# Revit family: Sarlam_Lighting_Bollard_light_Chartres_Infini_T1_vandal_resistant_Diam_322mm_2000Lm
name_source: partatom
category: Luminaires
units: mm (PartAtom-declared; Revit-internal decimal feet)

## family parameters
Basée sur le plan de construction = Non
Cote de connecteur circulaire = Utiliser le diamètre
Couper avec des vides une fois chargée = Non
Partagée = Non
Point de calcul de pièce = Non
Source d'éclairage = Non
Toujours verticalement = Oui
Type d'élément = Normal

## types (28) — shared parameters
Colour rendering index CRI = 80-89
Colour temperature K MAX = 4000
Colour temperature K MIN = 4000
Effective luminous flux lm = 2000
Fabricant = LEGRAND
General Conditions of Use = https://export.legrand.com
Height/depth = 70 mm  [stored 0.229659 ft]
Lamp holder = None
Lamp power at multiwatt = 21/39W
Lamp type = LED not exchangeable
Length = 322 mm  [stored 1.05643 ft]
Light sharing = Symmetric
Material housing = Plastique
Nominal voltage (Un) V MAX = 253
Nominal voltage (Un) V MIN = 207
Outer diameter = 322 mm  [stored 1.05643 ft]
Protection Class = II
Radiation angle = Open beam
Type of control gear = LED operating device current-controlled
URL = http://www.legrandoc.com
URL Bulkhead = http://www.legrandoc.com
Voltage type = AC
Width = 322 mm  [stored 1.05643 ft]
zero-valued in all types: Elévation par défaut

## per-type parameters (varying)
| type | Bollard light height | Bulkhead | Colour housing | Degree of protection (IP) | Description | Impact strength (IK) | Leg height | Modèle | Nominal current mA MAX | Nominal current mA MIN | System power W | Type of dimming | With light sensor | With movement sensor |
| Bollard light 600 + ON/OFF WHITE | 600 mm | Legrand-Lighting-Bulkhead-Chartres Infini-T1 Vandal resistant Diam 322mm-2000Lm : ON/OFF WHITE | LEGRAND - White | IP55 | BOLLARD LIGHT CHARTRES INFINI HEIGHT600 + CHARTRES INFINI 2000LM 4000K AV ON/OFF WHITE | IK10 | 524 mm | SL-532030 + SL-532024 | 131 | 106 | 27 | Not dimmable | Non | Non |
| Bollard light 1200 + ON/OFF WHITE | 1200 mm | Legrand-Lighting-Bulkhead-Chartres Infini-T1 Vandal resistant Diam 322mm-2000Lm : ON/OFF WHITE | LEGRAND - White | IP55 | BOLLARD LIGHT CHARTRES INFINI HEIGHT1200 + CHARTRES INFINI 2000LM 4000K AV ON/OFF WHITE | IK10 | 1124 mm  [stored 3.68766 ft] | SL-532033 + SL-532024 | 131 | 106 | 27 | Not dimmable | Non | Non |
| Bollard light 600 + ON/OFF ANTHRACITE | 600 mm | Legrand-Lighting-Bulkhead-Chartres Infini-T1 Vandal resistant Diam 322mm-2000Lm : ON/OFF ANTHRACITE | LEGRAND - Anthracite | IP55 | BOLLARD LIGHT CHARTRES INFINI HEIGHT600 + CHARTRES INFINI 2000LM 4000K AV ON/OFF BLACK | IK10 | 524 mm | SL-532031 + SL-532025 | 131 | 106 | 27 | Not dimmable | Non | Non |
| Bollard light 1200 + ON/OFF ANTHRACITE | 1200 mm | Legrand-Lighting-Bulkhead-Chartres Infini-T1 Vandal resistant Diam 322mm-2000Lm : ON/OFF ANTHRACITE | LEGRAND - Anthracite | IP55 | BOLLARD LIGHT CHARTRES INFINI HEIGHT1200 + CHARTRES INFINI 2000LM 4000K AV ON/OFF BLACK | IK10 | 1124 mm  [stored 3.68766 ft] | SL-532034 + SL-532025 | 131 | 106 | 27 | Not dimmable | Non | Non |
| Bollard light 600 + ON/OFF GREY METAL | 600 mm | Legrand-Lighting-Bulkhead-Chartres Infini-T1 Vandal resistant Diam 322mm-2000Lm : ON/OFF GREY METAL | LEGRAND - Grey | IP55 | BOLLARD LIGHT CHARTRES INFINI HEIGHT600 + CHARTRES INFINI 2000LM 4000K AV ON/OFF SILVER | IK10 | 524 mm | SL-532032 + SL-532026 | 131 | 106 | 27 | Not dimmable | Non | Non |
| Bollard light 1200 + ON/OFF GREY METAL | 1200 mm | Legrand-Lighting-Bulkhead-Chartres Infini-T1 Vandal resistant Diam 322mm-2000Lm : ON/OFF GREY METAL | LEGRAND - Grey | IP55 | BOLLARD LIGHT CHARTRES INFINI HEIGHT1200 + CHARTRES INFINI 2000LM 4000K STANDARD ON/OFF SILVER | IK10 | 1124 mm  [stored 3.68766 ft] | SL-532035 + SL-532026 | 131 | 106 | 27 | Not dimmable | Non | Non |
| Bollard light 600 + With microwave sensor WHITE | 600 mm | Legrand-Lighting-Bulkhead-Chartres Infini-T1 Vandal resistant Diam 322mm-2000Lm : With microwave sensor WHITE | LEGRAND - White | IP55 | BOLLARD LIGHT CHARTRES INFINI HEIGHT600 + CHARTRES INFINI 2000LM 4000K AV DETECTION HF WHITE | IK10 | 524 mm | SL-532030 + SL-532064 | 135 | 110 | 28 | Other | Oui | Oui |
| Bollard light 1200 + With microwave sensor WHITE | 1200 mm | Legrand-Lighting-Bulkhead-Chartres Infini-T1 Vandal resistant Diam 322mm-2000Lm : With microwave sensor WHITE | LEGRAND - White | IP55 | BOLLARD LIGHT CHARTRES INFINI HEIGHT1200 + CHARTRES INFINI 2000LM 4000K AV DETECTION HF WHITE | IK10 | 1124 mm  [stored 3.68766 ft] | SL-532033 + SL-532064 | 135 | 110 | 28 | Other | Oui | Oui |
| Bollard light 600 + With microwave sensor ANTHRACITE | 600 mm | Legrand-Lighting-Bulkhead-Chartres Infini-T1 Vandal resistant Diam 322mm-2000Lm : With microwave sensor ANTHRACITE | LEGRAND - Anthracite | IP55 | BOLLARD LIGHT CHARTRES INFINI HEIGHT600 + CHARTRES INFINI 2000LM 4000K AV DETECTION HF BLACK | IK10 | 524 mm | SL-532031 + SL-532065 | 135 | 110 | 28 | Other | Oui | Oui |
| Bollard light 1200 + With microwave sensor ANTHRACITE | 1200 mm | Legrand-Lighting-Bulkhead-Chartres Infini-T1 Vandal resistant Diam 322mm-2000Lm : With microwave sensor ANTHRACITE | LEGRAND - Anthracite | IP55 | BOLLARD LIGHT CHARTRES INFINI HEIGHT1200 + CHARTRES INFINI 2000LM 4000K AV DETECTION HF BLACK | IK10 | 1124 mm  [stored 3.68766 ft] | SL-532034 + SL-532065 | 135 | 110 | 28 | Other | Oui | Oui |
| Bollard light 600 + With microwave sensor GREY METAL | 600 mm | Legrand-Lighting-Bulkhead-Chartres Infini-T1 Vandal resistant Diam 322mm-2000Lm : With microwave sensor GREY METAL | LEGRAND - Grey | IP55 | BOLLARD LIGHT CHARTRES INFINI HEIGHT600 + CHARTRES INFINI 2000LM 4000K AV DETECTION HF SILVER | IK10 | 524 mm | SL-532032 + SL-532066 | 135 | 110 | 28 | Other | Oui | Oui |
| Bollard light 1200 + With microwave sensor GREY METAL | 1200 mm | Legrand-Lighting-Bulkhead-Chartres Infini-T1 Vandal resistant Diam 322mm-2000Lm : With microwave sensor GREY METAL | LEGRAND - Grey | IP55 | BOLLARD LIGHT CHARTRES INFINI HEIGHT1200 + CHARTRES INFINI 2000LM 4000K AV DETECTION HF SILVER | IK10 | 1124 mm  [stored 3.68766 ft] | SL-532035 + SL-532066 | 135 | 110 | 28 | Other | Oui | Oui |
| Bollard light 600 + With microwave sensor+clock WHITE | 600 mm | Legrand-Lighting-Bulkhead-Chartres Infini-T1 Vandal resistant Diam 322mm-2000Lm : With microwave sensor + clock WHITE | LEGRAND - White | IP55 | BOLLARD LIGHT CHARTRES INFINI HEIGHT600 + CHARTRES INFINI 2000LM 4000K  AV DETECTION HF + CLOCK WHITE | IK10 | 524 mm | SL-532030 + SL-532079 | 135 | 110 | 28 | Other | Oui | Oui |
| Bollard light 1200 + With microwave sensor+clock WHITE | 1200 mm | Legrand-Lighting-Bulkhead-Chartres Infini-T1 Vandal resistant Diam 322mm-2000Lm : With microwave sensor + clock WHITE | LEGRAND - White | IP55 | BOLLARD LIGHT CHARTRES INFINI HEIGHT1200 + CHARTRES INFINI 2000LM 4000K  AV DETECTION HF + CLOCK WHITE | IK10 | 1124 mm  [stored 3.68766 ft] | SL-532033 + SL-532079 | 135 | 110 | 28 | Other | Oui | Oui |
| Bollard light 600 + With microwave sensor+clock ANTHRACITE | 600 mm | Legrand-Lighting-Bulkhead-Chartres Infini-T1 Vandal resistant Diam 322mm-2000Lm : With microwave sensor + clock ANTHRACITE | LEGRAND - Anthracite | IP55 | BOLLARD LIGHT CHARTRES INFINI HEIGHT600 + CHARTRES INFINI 2000LM 4000K  AV DETECTION HF + CLOCK BLACK | IK10 | 524 mm | SL-532031 + SL-532080 | 135 | 110 | 28 | Other | Oui | Oui |
| Bollard light 1200 + With microwave sensor+clock ANTHRACITE | 1200 mm | Legrand-Lighting-Bulkhead-Chartres Infini-T1 Vandal resistant Diam 322mm-2000Lm : With microwave sensor + clock ANTHRACITE | LEGRAND - Anthracite | IP55 | BOLLARD LIGHT CHARTRES INFINI HEIGHT1200 + CHARTRES INFINI 2000LM 4000K  AV DETECTION HF + CLOCK BLACK | IK10 | 1124 mm  [stored 3.68766 ft] | SL-532034 + SL-532080 | 135 | 110 | 28 | Other | Oui | Oui |
| Bollard light 600 + With microwave sensor+clock GREY METAL | 600 mm | Legrand-Lighting-Bulkhead-Chartres Infini-T1 Vandal resistant Diam 322mm-2000Lm : With microwave sensor + clock GREY METAL | LEGRAND - Grey | IP55 | BOLLARD LIGHT CHARTRES INFINI HEIGHT600 + CHARTRES INFINI 2000LM 4000K  AV DETECTION HF + CLOCK SILVER | IK10 | 524 mm | SL-532032 + SL-532081 | 135 | 110 | 28 | Other | Oui | Oui |
| Bollard light 1200 + With microwave sensor+clock GREY METAL | 1200 mm | Legrand-Lighting-Bulkhead-Chartres Infini-T1 Vandal resistant Diam 322mm-2000Lm : With microwave sensor + clock GREY METAL | LEGRAND - Grey | IP55 | BOLLARD LIGHT CHARTRES INFINI HEIGHT1200 + CHARTRES INFINI 2000LM 4000K  AV DETECTION HF + CLOCK SILVER | IK10 | 1124 mm  [stored 3.68766 ft] | SL-532035 + SL-532081 | 135 | 110 | 28 | Other | Oui | Oui |
| Bollard light 600 + Double level / Timer WHITE | 600 mm | Legrand-Lighting-Bulkhead-Chartres Infini-T1 Vandal resistant Diam 322mm-2000Lm : Double level / Timer WHITE | LEGRAND - White | IP55 | BOLLARD LIGHT CHARTRES INFINI HEIGHT600 + CHARTRES INFINI 2000LM 4000K STD DOUBLE LEVEL / TIMER WHITE | IK10 | 524 mm | SL-532030 + SL-532090 | 135 | 110 | 28 | Other | Non | Non |
| Bollard light 1200 + Double level / Timer WHITE | 1200 mm | Legrand-Lighting-Bulkhead-Chartres Infini-T1 Vandal resistant Diam 322mm-2000Lm : Double level / Timer WHITE | LEGRAND - White | IP55 | BOLLARD LIGHT CHARTRES INFINI HEIGHT1200 + CHARTRES INFINI 2000LM 4000K AV DOUBLE LEVEL / TIMER WHITE | IK10 | 1124 mm  [stored 3.68766 ft] | SL-532033 + SL-532090 | 135 | 110 | 28 | Other | Non | Non |
| Bollard light 600 + Double level / Timer ANTHRACITE | 600 mm | Legrand-Lighting-Bulkhead-Chartres Infini-T1 Vandal resistant Diam 322mm-2000Lm : Double level / Timer ANTHRACITE | LEGRAND - Anthracite | IP55 | BORNE CHARTRES INFINI HAUTEUR 600 + CHARTRES INFINI 2000LM 4000K STD DOUBLE LEVEL / TIMER BLACK | IK10 | 524 mm | SL-532031 + SL-532091 | 135 | 110 | 28 | Other | Non | Non |
| Bollard light 1200 + Double level / Timer ANTHRACITE | 1200 mm | Legrand-Lighting-Bulkhead-Chartres Infini-T1 Vandal resistant Diam 322mm-2000Lm : Double level / Timer ANTHRACITE | LEGRAND - Anthracite | IP55 | BOLLARD LIGHT CHARTRES INFINI HEIGHT1200 + CHARTRES INFINI 2000LM 4000K AV DOUBLE LEVEL/TIMER BLACK | IK10 | 1124 mm  [stored 3.68766 ft] | SL-532034 + SL-532091 | 135 | 110 | 28 | Other | Non | Non |
| Bollard light 600 + Double level / Timer GREY METAL | 600 mm | Legrand-Lighting-Bulkhead-Chartres Infini-T1 Vandal resistant Diam 322mm-2000Lm : Double level / Timer GREY METAL | LEGRAND - Grey | IP55 | BOLLARD LIGHT CHARTRES INFINI HEIGHT600 + CHARTRES INFINI 2000LM 4000K AV DOUBLE LEVEL / TIMER SILVER | IK10 | 524 mm | SL-532032 + SL-532092 | 135 | 110 | 28 | Other | Non | Non |
| Bollard light 1200 + Double level / Timer GREY METAL | 1200 mm | Legrand-Lighting-Bulkhead-Chartres Infini-T1 Vandal resistant Diam 322mm-2000Lm : Double level / Timer GREY METAL | LEGRAND - Grey | IP55 | BOLLARD LIGHT CHARTRES INFINI HEIGHT1200 + CHARTRES INFINI 2000LM 4000K AV DOUBLE LEVEL / TIMER SILVER | IK10 | 1124 mm  [stored 3.68766 ft] | SL-532035 + SL-532092 | 135 | 110 | 28 | Other | Non | Non |
| Bollard light 1200 + Vandal resistant - With microwave sensor | 1200 mm | Legrand-Lighting-Bulkhead-Chartres Infini-T1 Vandal resistant Diam 322mm-2000Lm : Vandal resistant - With microwave sensor | LEGRAND - White | IP66 | BOLLARD LIGHT CHARTRES INFINI HEIGHT1200 + CHARTRES INFINI 2000LM 4000K SOLIROC DETECTION HF WHITE | IK10 | 1124 mm  [stored 3.68766 ft] | SL-532033 + SL-532097 | 135 | 110 | 27 | Other | Oui | Oui |
| Bollard light 600 + Vandal resistant - With microwave sensor | 600 mm | Legrand-Lighting-Bulkhead-Chartres Infini-T1 Vandal resistant Diam 322mm-2000Lm : Vandal resistant - With microwave sensor | LEGRAND - White | IP66 | BOLLARD LIGHT CHARTRES INFINI HEIGHT600 + CHARTRES INFINI 2000LM 4000K SOLIROC DETECTION HF WHITE | >IK10 | 524 mm | SL-532030 + SL-532097 | 135 | 110 | 28 | Other | Oui | Oui |
| Bollard light 1200 + Vandal resistant ON/OFF | 1200 mm | Legrand-Lighting-Bulkhead-Chartres Infini-T1 Vandal resistant Diam 322mm-2000Lm : Vandal resistant - ON/OFF | LEGRAND - White | IP66 | BOLLARD LIGHT CHARTRES INFINI HEIGHT1200 + CHARTRES INFINI 2000LM 4000K SOLIROC ON/OFF WHITE | >IK10 | 1124 mm  [stored 3.68766 ft] | SL-532033 + SL-532096 | 135 | 110 | 27 | Not dimmable | Non | Non |
| Bollard light 600 + Vandal resistant ON/OFF | 600 mm | Legrand-Lighting-Bulkhead-Chartres Infini-T1 Vandal resistant Diam 322mm-2000Lm : Vandal resistant - ON/OFF | LEGRAND - White | IP66 | BOLLARD LIGHT CHARTRES INFINI HEIGHT600 + CHARTRES INFINI 2000LM 4000K SOLIROC ON/OFF WHITE | >IK10 | 524 mm | SL-532030 + SL-532096 | 135 | 110 | 27 | Not dimmable | Non | Non |

note: [stored X ft] marks values corroborated as IEEE doubles in the binary element streams (Revit-internal decimal feet)

## geometry (parser evidence)
native form markers: Blend x14
no freeform markers — native parametric forms only
